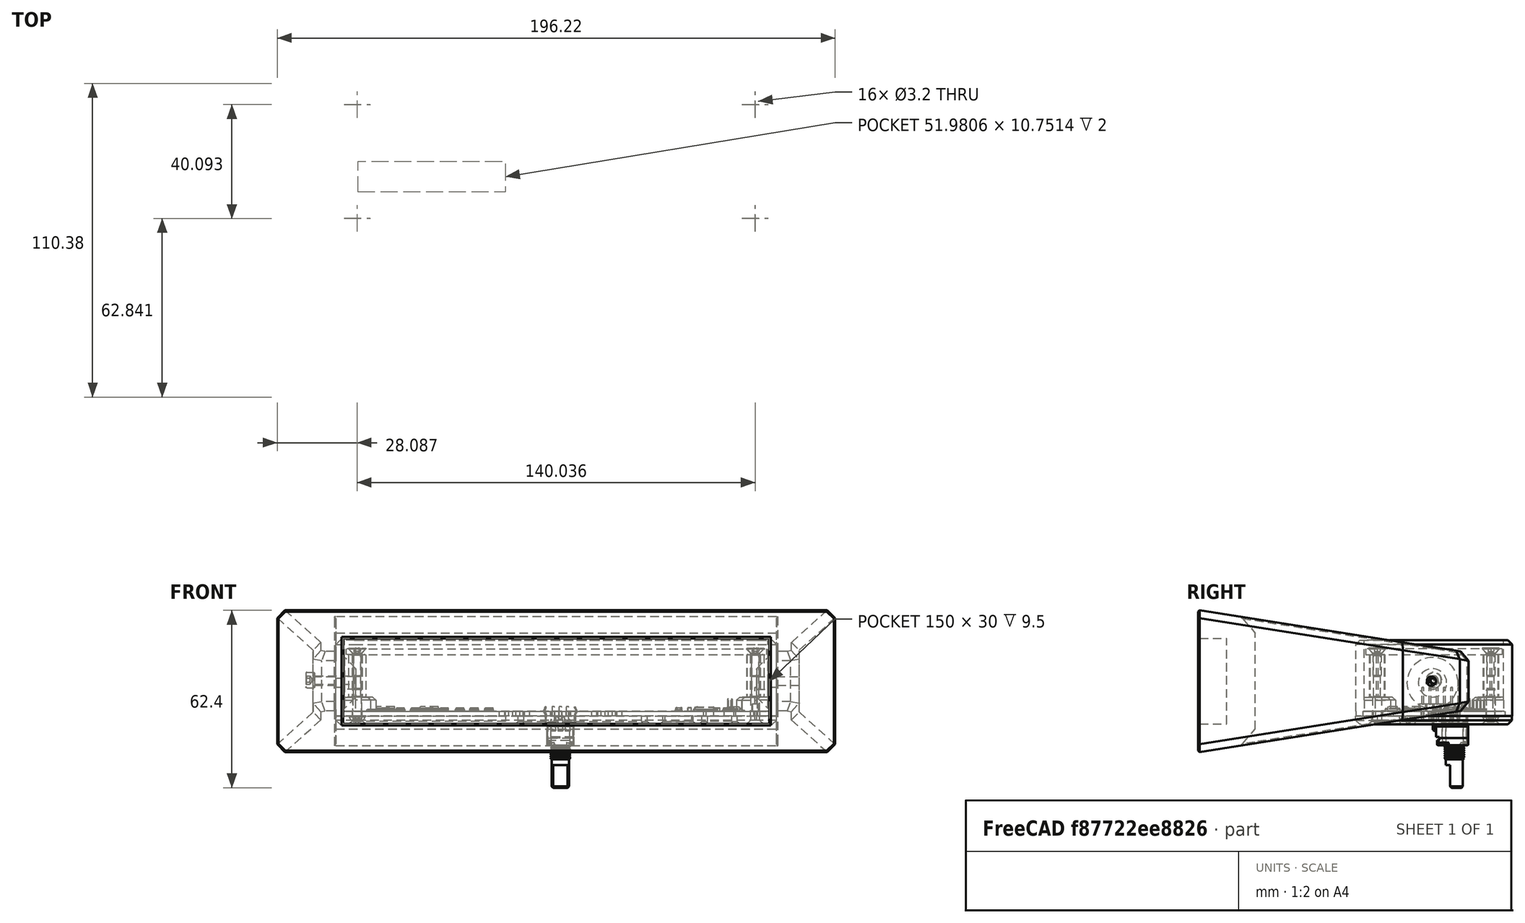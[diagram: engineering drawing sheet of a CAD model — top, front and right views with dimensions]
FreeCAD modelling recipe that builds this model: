
FCSTD DOCUMENT  (FreeCAD 0.19R24291 (Git))
Label: asm
License: All rights reserved
LicenseURL: http://en.wikipedia.org/wiki/All_rights_reserved
objects: Part::FeaturePython×19, PartDesign::CoordinateSystem×4
note: 23 computed .brp shape members not serialized (recipe doc carries the construction recipe); baked Part::Feature solids carry a one-line shape summary decoded from their .brp

FEATURE [PartDesign::CoordinateSystem] a2pLCS
  AttacherType = Attacher::AttachEngine3D
FEATURE [Part::FeaturePython] b_LCS_Collection_  label="LCS_Collection"  # WARN: FeaturePython — macro-defined, semantics opaque (R4)
  Group = -> [a2pLCS]
  Owner = b_pcb_001_
FEATURE [Part::FeaturePython] b_pcb_001_  label="pcb_001"  # a2plus imported part (geometry in sourceFile) (typed FeaturePython)
  a2p_Version = V0.1
  fixedPosition = true
  lcsLink = -> [b_LCS_Collection_]
  objectType = a2pPart
  sourceFile = ./pcb.FCStd
  subassemblyImport = false
  timeLastImport = 1.68843e+09
  updateColors = true
FEATURE [Part::FeaturePython] b_spacer_001_  label="spacer_Body_001"  # a2plus imported part (geometry in sourceFile) (typed FeaturePython)
  Placement = pos=(-2.47245,-52.5139,0.0146179) rot=(-1,0,0;1.5708rad)
  a2p_Version = V0.1
  fixedPosition = false
  objectType = a2pPart
  sourceFile = ./spacer.FCStd
  sourcePart = Body
  subassemblyImport = false
  timeLastImport = 1.68836e+09
  updateColors = true
FEATURE [PartDesign::CoordinateSystem] a2pLCS001
  AttacherType = Attacher::AttachEngine3D
FEATURE [Part::FeaturePython] b_LCS_Collection_001  label="LCS_Collection001"  # WARN: FeaturePython — macro-defined, semantics opaque (R4)
  Group = -> [a2pLCS001]
  Owner = CachedObject_0
FEATURE [Part::FeaturePython] PcbSpacer  label="M3x5.5x15-Spacer"  # WARN: FeaturePython — macro-defined, semantics opaque (R4)
  Placement = pos=(5,-5,5) rot=(0,0,1;0rad)
  diameter = 2
  invert = false
  length = 10
  offset = 0
  width = 1
FEATURE [PartDesign::CoordinateSystem] a2pLCS002
  AttacherType = Attacher::AttachEngine3D
FEATURE [Part::FeaturePython] b_LCS_Collection_002  label="LCS_Collection002"  # WARN: FeaturePython — macro-defined, semantics opaque (R4)
  Group = -> [a2pLCS002]
  Owner = CachedObject_0
FEATURE [Part::FeaturePython] b_cover_001_  label="cover_Body_001"  # a2plus imported part (geometry in sourceFile) (typed FeaturePython)
  Placement = pos=(-2.46663,-52.5489,-4.59344) rot=(-1,0,0;1.5708rad)
  a2p_Version = V0.1
  fixedPosition = false
  objectType = a2pPart
  sourceFile = ./cover.FCStd
  sourcePart = Body
  subassemblyImport = false
  timeLastImport = 1.68836e+09
  updateColors = true
FEATURE [Part::FeaturePython] PcbSpacer001  label="M3x5.5x15-Spacer001"  # WARN: FeaturePython — macro-defined, semantics opaque (R4)
  Placement = pos=(5,-45,5) rot=(0,0,1;0rad)
  diameter = 2
  invert = false
  length = 10
  offset = 0
  width = 1
FEATURE [Part::FeaturePython] PcbSpacer002  label="M3x5.5x15-Spacer002"  # WARN: FeaturePython — macro-defined, semantics opaque (R4)
  Placement = pos=(145.1,-45,5) rot=(0,0,1;0rad)
  diameter = 2
  invert = false
  length = 10
  offset = 0
  width = 1
FEATURE [Part::FeaturePython] PcbSpacer003  label="M3x5.5x15-Spacer003"  # WARN: FeaturePython — macro-defined, semantics opaque (R4)
  Placement = pos=(145.1,-5,5) rot=(0,0,1;0rad)
  diameter = 2
  invert = false
  length = 10
  offset = 0
  width = 1
FEATURE [Part::FeaturePython] b_led_plate_001_  label="led-plate_001"  # a2plus imported part (geometry in sourceFile) (typed FeaturePython)
  Placement = pos=(0.997033,-0.955639,22.011) rot=(1,0,0;1.5708rad)
  a2p_Version = V0.1
  fixedPosition = false
  objectType = a2pPart
  sourceFile = ./led-plate.FCStd
  subassemblyImport = false
  timeLastImport = 1.68836e+09
  updateColors = true
FEATURE [Part::FeaturePython] Screw004  label="M3x10-Screw"  # Fasteners workbench fastener (typed FeaturePython)
  Placement = pos=(5,-5,22.3) rot=(0,0,1;3.14159rad)
  diameter = 3
  invert = false
  length = 1
  lengthCustom = 10
  matchOuter = false
  offset = 0
  thread = false
  type = 18
FEATURE [Part::FeaturePython] Screw005  label="M3x10-Screw001"  # Fasteners workbench fastener (typed FeaturePython)
  Placement = pos=(5,-45,22.3) rot=(0,0,1;3.14159rad)
  diameter = 3
  invert = false
  length = 1
  lengthCustom = 10
  matchOuter = false
  offset = 0
  thread = false
  type = 18
FEATURE [Part::FeaturePython] Screw006  label="M3x10-Screw002"  # Fasteners workbench fastener (typed FeaturePython)
  Placement = pos=(145.1,-45,22.3) rot=(0,0,1;3.14159rad)
  diameter = 3
  invert = false
  length = 1
  lengthCustom = 10
  matchOuter = false
  offset = 0
  thread = false
  type = 18
FEATURE [Part::FeaturePython] Screw007  label="M3x10-Screw003"  # Fasteners workbench fastener (typed FeaturePython)
  Placement = pos=(145.1,-5,22.3) rot=(0,0,1;3.14159rad)
  diameter = 3
  invert = false
  length = 1
  lengthCustom = 10
  matchOuter = false
  offset = 0
  thread = false
  type = 18
FEATURE [Part::FeaturePython] b_stand_001_  label="stand_001"  # a2plus imported part (geometry in sourceFile) (typed FeaturePython)
  Placement = pos=(-2.48044,-87.8924,-14.3723) rot=(-1,0,0;1.5708rad)
  a2p_Version = V0.1
  fixedPosition = false
  objectType = a2pPart
  sourceFile = ./stand.FCStd
  subassemblyImport = false
  timeLastImport = 1.68836e+09
  updateColors = true
FEATURE [Part::FeaturePython] Screw008  label="M3x14-Screw"  # Fasteners workbench fastener (typed FeaturePython)
  Placement = pos=(-10,-25,11) rot=(0,1,0;4.71239rad)
  diameter = 4
  invert = false
  length = 5
  lengthCustom = 14
  matchOuter = false
  offset = 0
  thread = false
  type = 34
FEATURE [PartDesign::CoordinateSystem] a2pLCS003
  AttacherType = Attacher::AttachEngine3D
FEATURE [Part::FeaturePython] b_LCS_Collection_003  label="LCS_Collection003"  # WARN: FeaturePython — macro-defined, semantics opaque (R4)
  Group = -> [a2pLCS003]
  Owner = CachedObject_0
FEATURE [Part::FeaturePython] Screw  label="M3x10-Screw004"  # Fasteners workbench fastener (typed FeaturePython)
  Placement = pos=(5,-5,-2) rot=(1,0,0;3.14159rad)
  diameter = 1
  invert = false
  length = 2
  lengthCustom = 10
  matchOuter = false
  offset = 0
  thread = false
  type = 40
